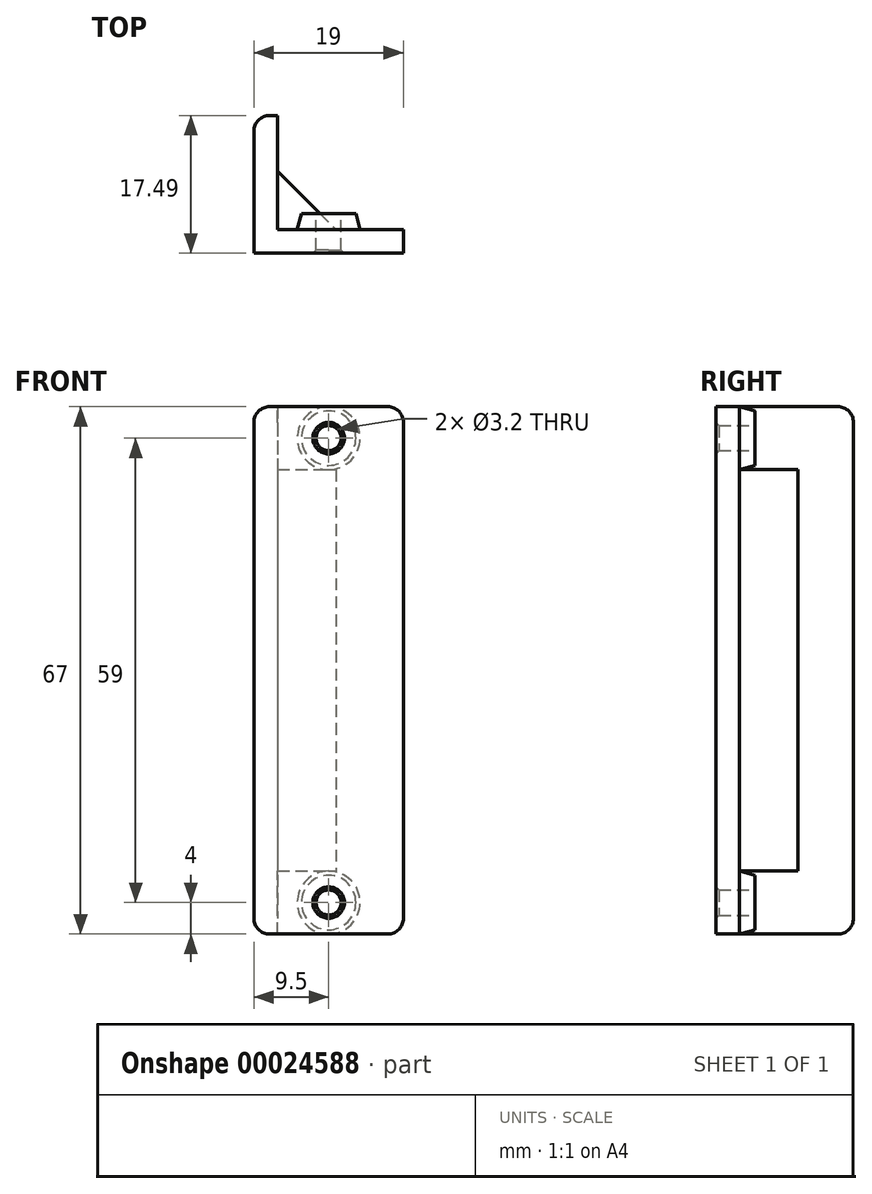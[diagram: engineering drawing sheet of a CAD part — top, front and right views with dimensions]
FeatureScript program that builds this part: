
annotation { "Feature Type Name" : "Feature", "Feature Type Description" : "" }
export const myFeature = defineFeature(function(context is Context, id is Id, definition is map)
    precondition{}
    {
        {
            var Q0;
            Q0=qCreatedBy(makeId("Top.planeOp"),FACE);
            var sketch = newSketch(context, id + "F0", { "sketchPlane" : qUnion([Q0])});
            skLineSegment(sketch, "E0", {"start": v(19, 0) * mm, "end": v(0, 0) * mm});
            skLineSegment(sketch, "E1", {"start": v(0, 0) * mm, "end": v(0, 17.49) * mm});
            skLineSegment(sketch, "E2", {"start": v(0, 17.49) * mm, "end": v(3, 17.49) * mm});
            skLineSegment(sketch, "E3", {"start": v(3, 17.49) * mm, "end": v(3, 10.42) * mm});
            skLineSegment(sketch, "E4", {"start": v(3, 10.42) * mm, "end": v(10.42, 3) * mm});
            skLineSegment(sketch, "E5", {"start": v(10.42, 3) * mm, "end": v(19, 3) * mm});
            skLineSegment(sketch, "E6", {"start": v(19, 3) * mm, "end": v(19, 0) * mm});
            skLineSegment(sketch, "E7", {"start": v(9.5, 10.11) * mm, "end": v(9.5, -4.35) * mm, "construction": true});
            skPoint(sketch, "E8", {"position": v(9.5, 0) * mm});
            skSolve(sketch);
        }
        {
            var Q0;
            Q0 = qSketchRegion(id + "F0", true);
            extrude(context, id + "F1", {"entities" : qUnion([Q0]), "depth" : 25.5 * mm});
        }
        {
            var Q0;
            Q0=makeQuery(id+"F1.opExtrude","CAP_FACE",FACE,{"disambiguationData":[OSD([sQuery(id+"F0.wireOp",EDGE,"E0"),sQuery(id+"F0.wireOp",EDGE,"E1"),sQuery(id+"F0.wireOp",EDGE,"E2"),sQuery(id+"F0.wireOp",EDGE,"E3"),sQuery(id+"F0.wireOp",EDGE,"E4"),sQuery(id+"F0.wireOp",EDGE,"E5"),sQuery(id+"F0.wireOp",EDGE,"E6")])],"isStart":false});
            var sketch = newSketch(context, id + "F2", { "sketchPlane" : qUnion([Q0])});
            skLineSegment(sketch, "E9", {"start": v(19, 3) * mm, "end": v(3, 3) * mm});
            skLineSegment(sketch, "E10", {"start": v(3, 3) * mm, "end": v(3, 17.49) * mm});
            skSolve(sketch);
        }
        {
            var Q0;
            Q0=makeQuery(id+"F2.imprint","IMPRINT",FACE,{"disambiguationData":[TD([[makeQuery(id+"F2.imprint","IMPRINT",EDGE,{"derivedFrom":makeQuery(id+"F1.opExtrude","CAP_EDGE",EDGE,{"disambiguationData":[OSD([sQuery(id+"F0.wireOp",EDGE,"E0")])],"isStart":false})}),-1.0]])]});
            extrude(context, id + "F3", {"entities" : qUnion([Q0]), "operationType" : NewBodyOperationType.ADD, "depth" : 8 * mm});
        }
        {
            var Q0;
            Q0=makeQuery(id+"F3.boolean.opBoolean","MERGE",FACE,{"derivedFrom":[makeQuery(id+"F1.opExtrude","SWEPT_FACE",FACE,{"disambiguationData":[OSD([sQuery(id+"F0.wireOp",EDGE,"E5")])]}),makeQuery(id+"F3.opExtrude","SWEPT_FACE",FACE,{"disambiguationData":[OSD([sQuery(id+"F2.wireOp",EDGE,"E9")])]})]});
            var sketch = newSketch(context, id + "F4", { "sketchPlane" : qUnion([Q0])});
            skLineSegment(sketch, "E11.0", {"start": v(0, 33.5) * mm, "end": v(0, 0) * mm, "construction": true});
            skPoint(sketch, "E12", {"position": v(-3, 29.5) * mm});
            skLineSegment(sketch, "E13", {"start": v(0, 29.5) * mm, "end": v(-19, 29.5) * mm, "construction": true});
            skPoint(sketch, "E14", {"position": v(-9.5, 29.5) * mm});
            skCircle(sketch, "E15", {"center": v(-9.5, 29.5) * mm, "radius": 4 * mm});
            skSolve(sketch);
        }
        {
            var Q0;
            Q0 = qSketchRegion(id + "F4", true);
            extrude(context, id + "F5", {"entities" : qUnion([Q0]), "operationType" : NewBodyOperationType.ADD, "depth" : 2 * mm, "hasDraft" : true, "draftAngle" : 15 * degree, "draftPullDirection" : true});
        }
        {
            var Q0;
            Q0=makeQuery(id+"F5.opExtrude","CAP_FACE",FACE,{"disambiguationData":[OSD([sQuery(id+"F4.wireOp",EDGE,"E15")])],"isStart":false});
            var sketch = newSketch(context, id + "F6", { "sketchPlane" : qUnion([Q0])});
            skCircle(sketch, "E16.0", {"center": v(-9.5, 29.5) * mm, "radius": 3.46 * mm, "construction": true});
            skCircle(sketch, "E17", {"center": v(-9.5, 29.5) * mm, "radius": 1.6 * mm});
            skSolve(sketch);
        }
        {
            var Q0;
            Q0 = qSketchRegion(id + "F6", true);
            extrude(context, id + "F7", {"entities" : qUnion([Q0]), "operationType" : NewBodyOperationType.REMOVE, "endBound" : BoundingType.THROUGH_ALL, "oppositeDirection" : true, "depth" : 25 * mm});
        }
        {
            var Q0;
            {var subQ0=sQuery(id+"F0.wireOp",EDGE,"E0");Q0=makeQuery(id+"F7.boolean.opBoolean","INTERSECT",EDGE,{"derivedFrom":[makeQuery(id+"F3.boolean.opBoolean","MERGE",FACE,{"derivedFrom":[makeQuery(id+"F1.opExtrude","SWEPT_FACE",FACE,{"disambiguationData":[OSD([subQ0])]}),makeQuery(id+"F3.opExtrude","SWEPT_FACE",FACE,{"disambiguationData":[OSD([subQ0])]})]}),makeQuery(id+"F7.opExtrude","SWEPT_FACE",FACE,{"disambiguationData":[OSD([sQuery(id+"F6.wireOp",EDGE,"E17")])]})]});}
            chamfer(context, id + "F8", {"entities" : qUnion([Q0]), "width" : 0.4 * mm});
        }
        {
            var Q0;
            Q0=makeQuery(id+"F1.opExtrude","SWEPT_BODY",BODY,{"disambiguationData":[OSD([sQuery(id+"F0.wireOp",EDGE,"E0"),sQuery(id+"F0.wireOp",EDGE,"E1"),sQuery(id+"F0.wireOp",EDGE,"E2"),sQuery(id+"F0.wireOp",EDGE,"E3"),sQuery(id+"F0.wireOp",EDGE,"E4"),sQuery(id+"F0.wireOp",EDGE,"E5"),sQuery(id+"F0.wireOp",EDGE,"E6")])]});
            var Q1;
            Q1=qCreatedBy(makeId("Top.planeOp"),FACE);
            mirror(context, id + "F9", {"operationType" : NewBodyOperationType.ADD, "entities" : qUnion([Q0]), "mirrorPlane" : qUnion([Q1])});
        }
        {
            var Q0;
            {var subQ0=sQuery(id+"F0.wireOp",EDGE,"E2");var subQ1=sQuery(id+"F0.wireOp",EDGE,"E1");var subQ2=makeQuery(id+"F3.boolean.opBoolean","MERGE",EDGE,{"derivedFrom":[makeQuery(id+"F1.opExtrude","SWEPT_EDGE",EDGE,{"disambiguationData":[OSD([subQ1,subQ0])]}),makeQuery(id+"F3.opExtrude","SWEPT_EDGE",EDGE,{"disambiguationData":[OSD([subQ1,subQ0])]})]});Q0=makeQuery(id+"F9.boolean.opBoolean","MERGE",EDGE,{"derivedFrom":[subQ2,makeQuery(id+"F9.opPattern","COPY",EDGE,{"derivedFrom":subQ2,"instanceName":"1"})]});}
            var Q1;
            Q1=makeQuery(id+"F9.opPattern","COPY",EDGE,{"derivedFrom":makeQuery(id+"F3.opExtrude","CAP_EDGE",EDGE,{"disambiguationData":[OSD([sQuery(id+"F0.wireOp",EDGE,"E1")])],"isStart":false}),"instanceName":"1"});
            var Q2;
            Q2=makeQuery(id+"F9.opPattern","COPY",EDGE,{"derivedFrom":makeQuery(id+"F3.opExtrude","CAP_EDGE",EDGE,{"disambiguationData":[OSD([sQuery(id+"F0.wireOp",EDGE,"E2")])],"isStart":false}),"instanceName":"1"});
            var Q3;
            Q3=makeQuery(id+"F3.opExtrude","CAP_EDGE",EDGE,{"disambiguationData":[OSD([sQuery(id+"F0.wireOp",EDGE,"E2")])],"isStart":false});
            var Q4;
            Q4=makeQuery(id+"F3.opExtrude","CAP_EDGE",EDGE,{"disambiguationData":[OSD([sQuery(id+"F0.wireOp",EDGE,"E1")])],"isStart":false});
            var Q5;
            Q5=makeQuery(id+"F3.opExtrude","CAP_EDGE",EDGE,{"disambiguationData":[OSD([sQuery(id+"F0.wireOp",EDGE,"E6")])],"isStart":false});
            var Q6;
            Q6=makeQuery(id+"F9.opPattern","COPY",EDGE,{"derivedFrom":makeQuery(id+"F3.opExtrude","CAP_EDGE",EDGE,{"disambiguationData":[OSD([sQuery(id+"F0.wireOp",EDGE,"E6")])],"isStart":false}),"instanceName":"1"});
            fillet(context, id + "F10", {"entities" : qUnion([Q0, Q1, Q2, Q3, Q4, Q5, Q6]), "radius" : 2 * mm, "allowEdgeOverflow" : false});
        }
    });
